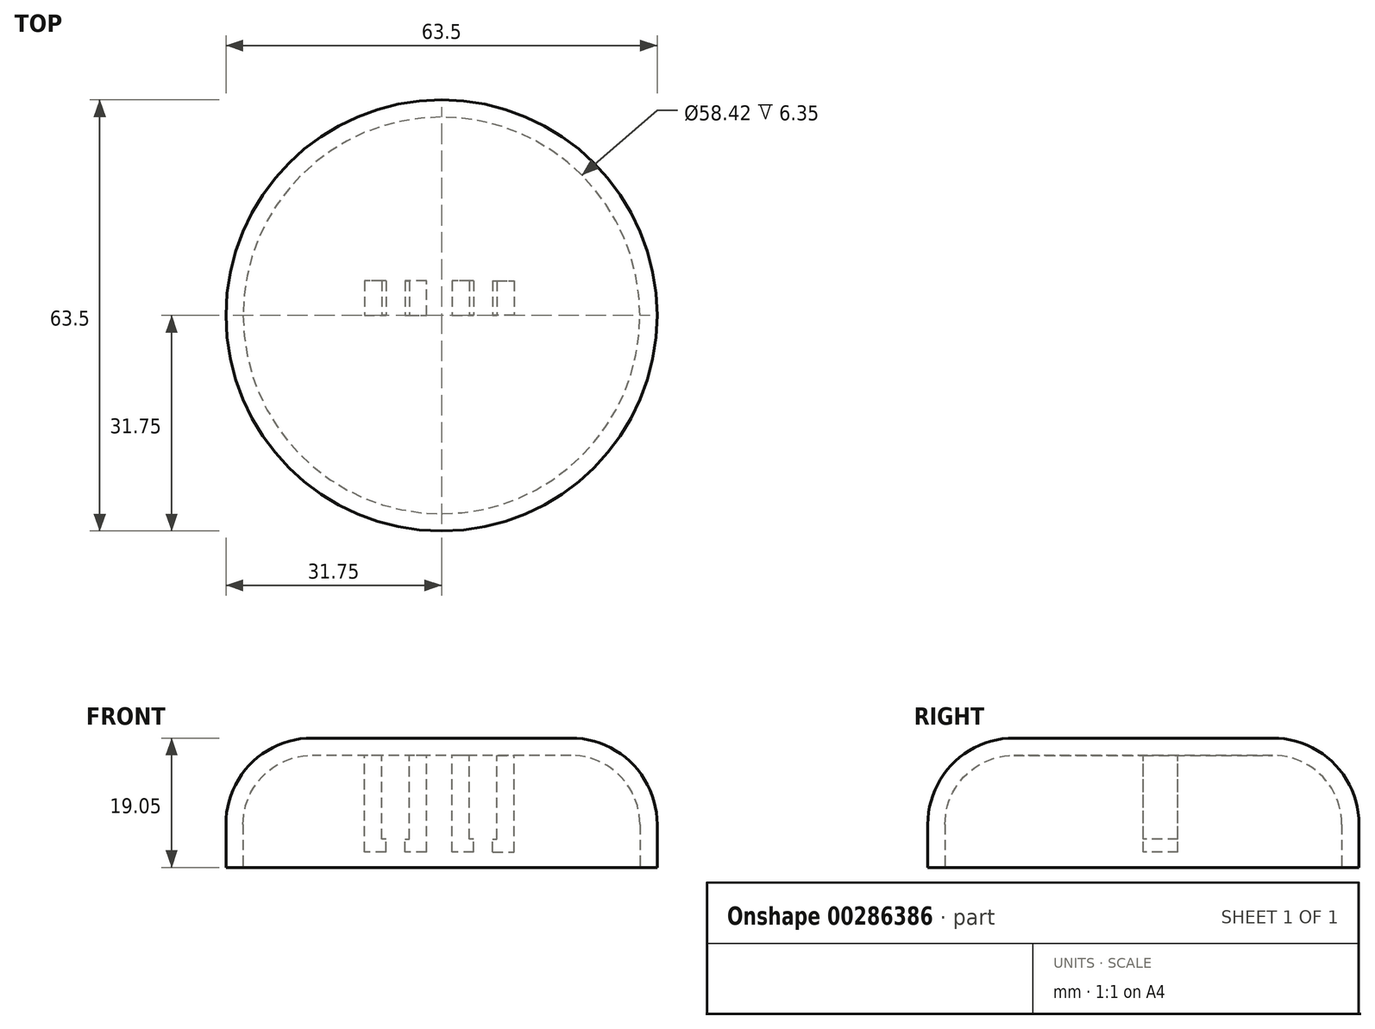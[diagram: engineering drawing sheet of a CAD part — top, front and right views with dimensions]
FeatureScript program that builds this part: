
annotation { "Feature Type Name" : "Feature", "Feature Type Description" : "" }
export const myFeature = defineFeature(function(context is Context, id is Id, definition is map)
    precondition{}
    {
        {
            var Q0;
            Q0=qCreatedBy(makeId("Top.planeOp"),FACE);
            var sketch = newSketch(context, id + "F0", { "sketchPlane" : qUnion([Q0])});
            skCircle(sketch, "E0", {"center": v(0, 0) * mm, "radius": 31.75 * mm});
            skSolve(sketch);
        }
        {
            var Q0;
            Q0 = qSketchRegion(id + "F0", true);
            extrude(context, id + "F1", {"entities" : qUnion([Q0]), "depth" : 19.05 * mm});
        }
        {
            var Q0;
            Q0=makeQuery(id+"F1.opExtrude","CAP_EDGE",EDGE,{"disambiguationData":[OSD([sQuery(id+"F0.wireOp",EDGE,"E0")])],"isStart":false});
            fillet(context, id + "F2", {"entities" : qUnion([Q0]), "radius" : 12.7 * mm, "tangentPropagation" : true, "allowEdgeOverflow" : false});
        }
        {
            var Q0;
            Q0=makeQuery(id+"F1.opExtrude","CAP_FACE",FACE,{"disambiguationData":[OSD([sQuery(id+"F0.wireOp",EDGE,"E0")])],"isStart":true});
            shell(context, id + "F3", {"entities" : qUnion([Q0]), "thickness" : 2.54 * mm});
        }
        {
            var Q0;
            {var subQ0=sQuery(id+"F0.wireOp",EDGE,"E0");Q0=makeQuery(id+"F3.opShell","OFFSET_FACE",FACE,{"disambiguationData":[OSD([subQ0]),TDD([makeQuery(id+"F1.opExtrude","CAP_FACE",FACE,{"disambiguationData":[OSD([subQ0])],"isStart":false})])]});}
            var sketch = newSketch(context, id + "F4", { "sketchPlane" : qUnion([Q0])});
            skSolve(sketch);
        }
        {
            var Q0;
            {var subQ0=sQuery(id+"F0.wireOp",EDGE,"E0");Q0=makeQuery(id+"F4.imprint","IMPRINT",FACE,{"disambiguationData":[TD([[makeQuery(id+"F4.imprint","IMPRINT",EDGE,{"derivedFrom":makeQuery(id+"F3.opShell","OFFSET_EDGE",EDGE,{"disambiguationData":[OSD([subQ0]),TDD([makeQuery(id+"F2.opFillet","BLEND_EDGE",EDGE,{"blendedFrom":[makeQuery(id+"F1.opExtrude","CAP_EDGE",EDGE,{"disambiguationData":[OSD([subQ0])],"isStart":false}),makeQuery(id+"F1.opExtrude","CAP_FACE",FACE,{"disambiguationData":[OSD([subQ0])],"isStart":false})],"blendedInto":[makeQuery(id+"F1.opExtrude","CAP_FACE",FACE,{"disambiguationData":[OSD([subQ0])],"isStart":false})]})])]})}),-1.0]])]});}
            var sketch = newSketch(context, id + "F5", { "sketchPlane" : qUnion([Q0])});
            skLineSegment(sketch, "E1", {"start": v(8.18, -5.08) * mm, "end": v(8.18, 0) * mm});
            skLineSegment(sketch, "E2", {"start": v(4.12, -5.08) * mm, "end": v(4.12, 0) * mm});
            skLineSegment(sketch, "E3", {"start": v(-4.76, -5.08) * mm, "end": v(-4.76, 0) * mm});
            skLineSegment(sketch, "E4", {"start": v(-8.82, -5.08) * mm, "end": v(-8.82, 0) * mm});
            skLineSegment(sketch, "E5", {"start": v(8.18, -5.08) * mm, "end": v(10.72, -5.08) * mm});
            skLineSegment(sketch, "E6", {"start": v(10.72, -5.08) * mm, "end": v(10.72, 0) * mm});
            skLineSegment(sketch, "E7", {"start": v(10.72, 0) * mm, "end": v(8.18, 0) * mm});
            skLineSegment(sketch, "E8", {"start": v(4.12, -5.08) * mm, "end": v(1.58, -5.08) * mm});
            skLineSegment(sketch, "E9", {"start": v(1.58, -5.08) * mm, "end": v(1.58, 0) * mm});
            skLineSegment(sketch, "E10", {"start": v(1.58, 0) * mm, "end": v(4.12, 0) * mm});
            skLineSegment(sketch, "E11", {"start": v(-4.76, 0) * mm, "end": v(-2.22, 0) * mm});
            skLineSegment(sketch, "E12", {"start": v(-2.22, 0) * mm, "end": v(-2.22, -5.08) * mm});
            skLineSegment(sketch, "E13", {"start": v(-2.22, -5.08) * mm, "end": v(-4.76, -5.08) * mm});
            skLineSegment(sketch, "E14", {"start": v(-8.82, -5.08) * mm, "end": v(-11.36, -5.08) * mm});
            skLineSegment(sketch, "E15", {"start": v(-11.36, -5.08) * mm, "end": v(-11.36, 0) * mm});
            skLineSegment(sketch, "E16", {"start": v(-11.36, 0) * mm, "end": v(-8.82, 0) * mm});
            skSolve(sketch);
        }
        {
            var Q0;
            Q0 = qSketchRegion(id + "F5", true);
            extrude(context, id + "F6", {"entities" : qUnion([Q0]), "operationType" : NewBodyOperationType.ADD, "depth" : 14.22 * mm});
        }
        {
            var Q0;
            Q0=makeQuery(id+"F6.opExtrude","SWEPT_FACE",FACE,{"disambiguationData":[OSD([sQuery(id+"F5.wireOp",EDGE,"E1")])]});
            var sketch = newSketch(context, id + "F7", { "sketchPlane" : qUnion([Q0])});
            skLineSegment(sketch, "E17", {"start": v(-5.08, 2.29) * mm, "end": v(0, 2.29) * mm});
            skLineSegment(sketch, "E18", {"start": v(0, 2.29) * mm, "end": v(0, 4.2) * mm});
            skLineSegment(sketch, "E19", {"start": v(0, 4.2) * mm, "end": v(-5.08, 4.2) * mm});
            skLineSegment(sketch, "E20", {"start": v(-5.08, 4.2) * mm, "end": v(-5.08, 2.29) * mm});
            skSolve(sketch);
        }
        {
            var Q0;
            Q0 = qSketchRegion(id + "F7", true);
            extrude(context, id + "F8", {"entities" : qUnion([Q0]), "operationType" : NewBodyOperationType.ADD, "depth" : 0.64 * mm});
        }
        {
            var Q0;
            Q0=makeQuery(id+"F6.opExtrude","SWEPT_FACE",FACE,{"disambiguationData":[OSD([sQuery(id+"F5.wireOp",EDGE,"E2")])]});
            var sketch = newSketch(context, id + "F9", { "sketchPlane" : qUnion([Q0])});
            skLineSegment(sketch, "E21", {"start": v(5.08, 2.29) * mm, "end": v(5.08, 4.2) * mm});
            skLineSegment(sketch, "E22", {"start": v(5.08, 4.2) * mm, "end": v(0, 4.2) * mm});
            skLineSegment(sketch, "E23", {"start": v(0, 4.2) * mm, "end": v(0, 2.29) * mm});
            skLineSegment(sketch, "E24", {"start": v(0, 2.29) * mm, "end": v(5.08, 2.29) * mm});
            skSolve(sketch);
        }
        {
            var Q0;
            Q0 = qSketchRegion(id + "F9", true);
            extrude(context, id + "F10", {"entities" : qUnion([Q0]), "operationType" : NewBodyOperationType.ADD, "depth" : 0.64 * mm});
        }
        {
            var Q0;
            Q0=makeQuery(id+"F6.opExtrude","SWEPT_FACE",FACE,{"disambiguationData":[OSD([sQuery(id+"F5.wireOp",EDGE,"E3")])]});
            var sketch = newSketch(context, id + "F11", { "sketchPlane" : qUnion([Q0])});
            skLineSegment(sketch, "E25", {"start": v(-5.08, 2.29) * mm, "end": v(0, 2.29) * mm});
            skLineSegment(sketch, "E26", {"start": v(0, 2.29) * mm, "end": v(0, 4.2) * mm});
            skLineSegment(sketch, "E27", {"start": v(0, 4.2) * mm, "end": v(-5.08, 4.2) * mm});
            skLineSegment(sketch, "E28", {"start": v(-5.08, 4.2) * mm, "end": v(-5.08, 2.29) * mm});
            skSolve(sketch);
        }
        {
            var Q0;
            Q0 = qSketchRegion(id + "F11", true);
            extrude(context, id + "F12", {"entities" : qUnion([Q0]), "operationType" : NewBodyOperationType.ADD, "depth" : 0.64 * mm});
        }
        {
            var Q0;
            Q0=makeQuery(id+"F6.opExtrude","SWEPT_FACE",FACE,{"disambiguationData":[OSD([sQuery(id+"F5.wireOp",EDGE,"E4")])]});
            var sketch = newSketch(context, id + "F13", { "sketchPlane" : qUnion([Q0])});
            skLineSegment(sketch, "E29", {"start": v(5.08, 2.29) * mm, "end": v(5.08, 4.2) * mm});
            skLineSegment(sketch, "E30", {"start": v(5.08, 4.2) * mm, "end": v(0, 4.2) * mm});
            skLineSegment(sketch, "E31", {"start": v(0, 4.2) * mm, "end": v(0, 2.29) * mm});
            skLineSegment(sketch, "E32", {"start": v(0, 2.29) * mm, "end": v(5.08, 2.29) * mm});
            skSolve(sketch);
        }
        {
            var Q0;
            Q0 = qSketchRegion(id + "F13", true);
            extrude(context, id + "F14", {"entities" : qUnion([Q0]), "operationType" : NewBodyOperationType.ADD, "depth" : 0.64 * mm});
        }
    });
